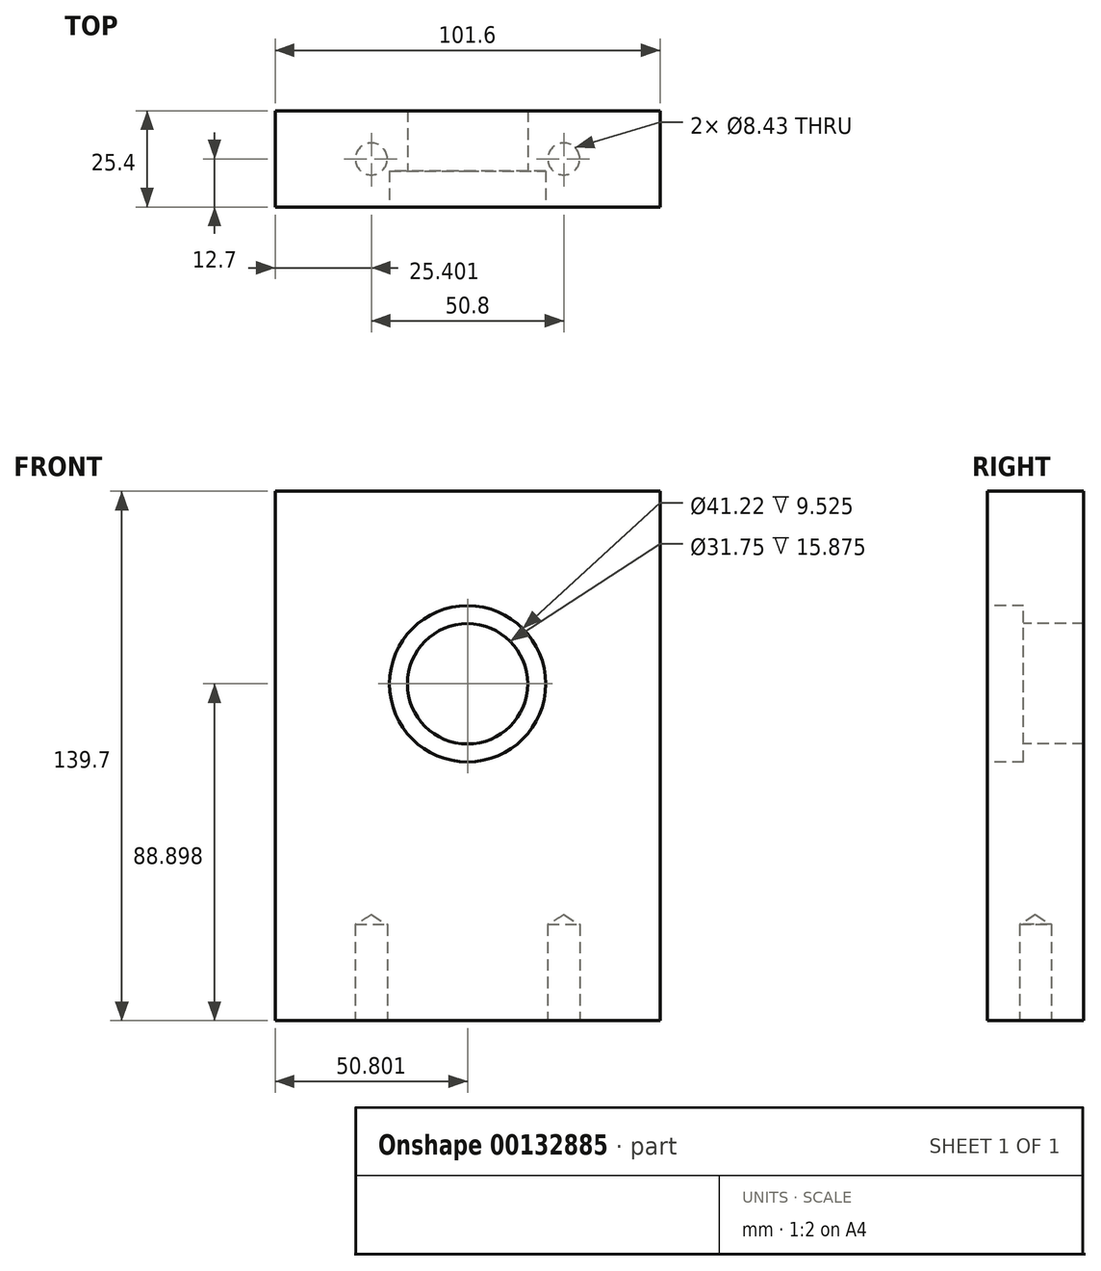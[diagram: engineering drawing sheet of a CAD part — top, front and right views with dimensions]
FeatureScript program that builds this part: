
annotation { "Feature Type Name" : "Feature", "Feature Type Description" : "" }
export const myFeature = defineFeature(function(context is Context, id is Id, definition is map)
    precondition{}
    {
        {
            var Q0;
            Q0=qCreatedBy(makeId("Front.planeOp"),FACE);
            var sketch = newSketch(context, id + "F0", { "sketchPlane" : qUnion([Q0])});
            skLineSegment(sketch, "E0.bottom", {"start": v(-41.79, 67.43) * mm, "end": v(59.81, 67.43) * mm});
            skLineSegment(sketch, "E0.top", {"start": v(-41.79, -72.27) * mm, "end": v(59.81, -72.27) * mm});
            skLineSegment(sketch, "E0.left", {"start": v(-41.79, 67.43) * mm, "end": v(-41.79, -72.27) * mm});
            skLineSegment(sketch, "E0.right", {"start": v(59.81, 67.43) * mm, "end": v(59.81, -72.27) * mm});
            skSolve(sketch);
        }
        {
            var Q0;
            Q0=makeQuery(id+"F0.imprint","IMPRINT",FACE,{"disambiguationData":[TD([[makeQuery(id+"F0.imprint","IMPRINT",EDGE,{"derivedFrom":sQuery(id+"F0.wireOp",EDGE,"E0.bottom")}),-1.0]])]});
            extrude(context, id + "F1", {"entities" : qUnion([Q0]), "depth" : 25.4 * mm});
        }
        {
            var Q0;
            Q0=makeQuery(id+"F1.opExtrude","SWEPT_FACE",FACE,{"disambiguationData":[OSD([sQuery(id+"F0.wireOp",EDGE,"E0.top")])]});
            var sketch = newSketch(context, id + "F2", { "sketchPlane" : qUnion([Q0])});
            skPoint(sketch, "E1", {"position": v(-16.39, 12.7) * mm});
            skPoint(sketch, "E2", {"position": v(34.41, 12.7) * mm});
            skSolve(sketch);
        }
        {
            var Q0;
            Q0=sQuery(id+"F2.wireOp",VERTEX,"E1");
            var Q1;
            Q1=sQuery(id+"F2.wireOp",VERTEX,"E2");
            var Q2;
            Q2=makeQuery(id+"F1.opExtrude","SWEPT_BODY",BODY,{"disambiguationData":[OSD([sQuery(id+"F0.wireOp",EDGE,"E0.bottom"),sQuery(id+"F0.wireOp",EDGE,"E0.top"),sQuery(id+"F0.wireOp",EDGE,"E0.left"),sQuery(id+"F0.wireOp",EDGE,"E0.right")])]});
            hole(context, id + "F3", {"style" : HoleStyle.SIMPLE, "endStyle" : HoleEndStyle.BLIND, "standardTappedOrClearance" : lookupTablePath({ "standard" : "ANSI", "engagement" : "75%", "pitch" : "24 tpi", "size" : "3/8", "type" : "Tapped" }), "standardBlindInLast" : lookupTablePath({ "standard" : "ANSI", "engagement" : "75%", "pitch" : "24 tpi", "size" : "3/8", "type" : "Tapped" }), "holeDiameter" : 8.43 * mm, "holeDepth" : 25.4 * mm, "locations" : qUnion([Q0, Q1]), "scope" : qUnion([Q2]), "majorDiameter" : 9.53 * mm});
        }
        {
            var Q0;
            Q0=makeQuery(id+"F1.opExtrude","CAP_FACE",FACE,{"disambiguationData":[OSD([sQuery(id+"F0.wireOp",EDGE,"E0.bottom"),sQuery(id+"F0.wireOp",EDGE,"E0.top"),sQuery(id+"F0.wireOp",EDGE,"E0.left"),sQuery(id+"F0.wireOp",EDGE,"E0.right")])],"isStart":false});
            var sketch = newSketch(context, id + "F4", { "sketchPlane" : qUnion([Q0])});
            skCircle(sketch, "E3", {"center": v(9.01, 16.63) * mm, "radius": 20.61 * mm});
            skSolve(sketch);
        }
        {
            var Q0;
            Q0=makeQuery(id+"F4.imprint","IMPRINT",FACE,{"disambiguationData":[TD([[makeQuery(id+"F4.imprint","IMPRINT",EDGE,{"derivedFrom":sQuery(id+"F4.wireOp",EDGE,"E3")}),1.0]])]});
            extrude(context, id + "F5", {"entities" : qUnion([Q0]), "operationType" : NewBodyOperationType.REMOVE, "oppositeDirection" : true, "depth" : 9.52 * mm});
        }
        {
            var Q0;
            Q0=makeQuery(id+"F5.boolean.opBoolean","COPY",FACE,{"derivedFrom":makeQuery(id+"F5.opExtrude","CAP_FACE",FACE,{"disambiguationData":[OSD([sQuery(id+"F4.wireOp",EDGE,"E3")])],"isStart":false})});
            var sketch = newSketch(context, id + "F6", { "sketchPlane" : qUnion([Q0])});
            skCircle(sketch, "E4", {"center": v(9.01, 16.63) * mm, "radius": 15.88 * mm});
            skSolve(sketch);
        }
        {
            var Q0;
            Q0=makeQuery(id+"F6.imprint","IMPRINT",FACE,{"disambiguationData":[TD([[makeQuery(id+"F6.imprint","IMPRINT",EDGE,{"derivedFrom":sQuery(id+"F6.wireOp",EDGE,"E4")}),1.0]])]});
            extrude(context, id + "F7", {"entities" : qUnion([Q0]), "operationType" : NewBodyOperationType.REMOVE, "oppositeDirection" : true, "depth" : 25.4 * mm});
        }
    });
